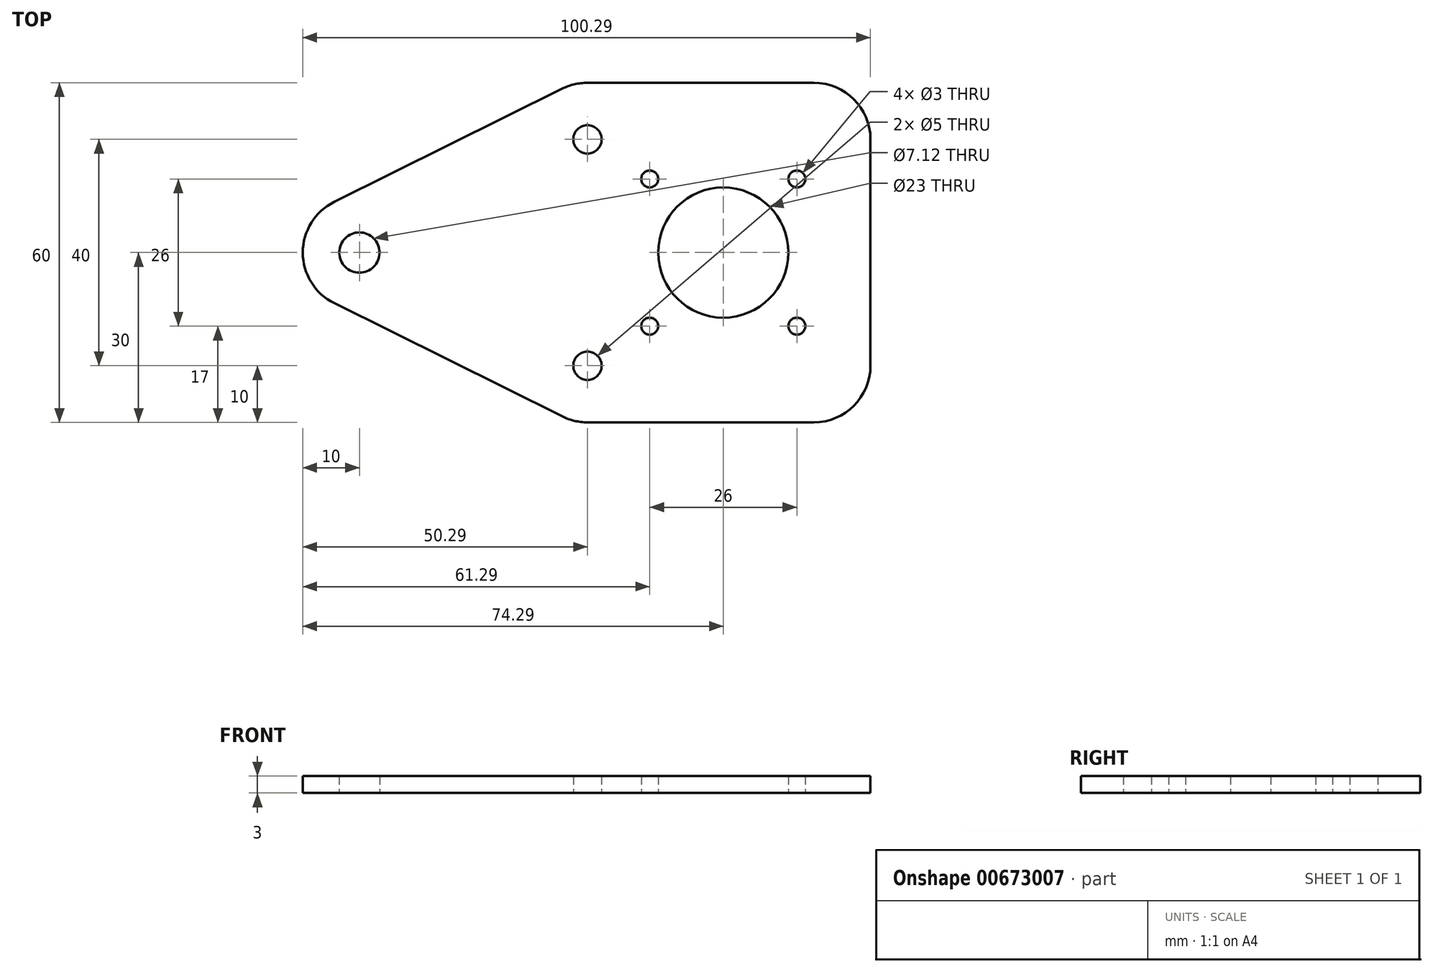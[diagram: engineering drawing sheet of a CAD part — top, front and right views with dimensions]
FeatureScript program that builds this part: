
annotation { "Feature Type Name" : "Feature", "Feature Type Description" : "" }
export const myFeature = defineFeature(function(context is Context, id is Id, definition is map)
    precondition{}
    {
        {
            var Q0;
            Q0=qCreatedBy(makeId("Top.planeOp"),FACE);
            var sketch = newSketch(context, id + "F0", { "sketchPlane" : qUnion([Q0])});
            skCircle(sketch, "E0", {"center": v(0, 0) * mm, "radius": 2.5 * mm});
            skCircle(sketch, "E1", {"center": v(0, 40) * mm, "radius": 2.5 * mm});
            skLineSegment(sketch, "E2", {"start": v(0, 40) * mm, "end": v(0, 0) * mm, "construction": true});
            skLineSegment(sketch, "E3", {"start": v(0, 20) * mm, "end": v(-40.3, 20) * mm, "construction": true});
            skCircle(sketch, "E4", {"center": v(-40.3, 20) * mm, "radius": 3.56 * mm});
            skArc(sketch, "E5", {"start": v(0, 50) * mm, "mid": v(-2.28, 49.74) * mm, "end": v(-4.45, 48.96) * mm});
            skArc(sketch, "E6", {"start": v(-4.45, -8.96) * mm, "mid": v(-2.28, -9.74) * mm, "end": v(0, -10) * mm});
            skArc(sketch, "E7", {"start": v(-44.74, 28.96) * mm, "mid": v(-50.3, 20) * mm, "end": v(-44.74, 11.04) * mm});
            skLineSegment(sketch, "E8", {"start": v(-44.74, 28.96) * mm, "end": v(-4.45, 48.96) * mm});
            skLineSegment(sketch, "E9", {"start": v(-44.74, 11.04) * mm, "end": v(-4.45, -8.96) * mm});
            skLineSegment(sketch, "E10", {"start": v(0, 40) * mm, "end": v(40, 40) * mm, "construction": true});
            skLineSegment(sketch, "E11", {"start": v(0, 0) * mm, "end": v(40, 0) * mm, "construction": true});
            skArc(sketch, "E12", {"start": v(50, 40) * mm, "mid": v(47.07, 47.07) * mm, "end": v(40, 50) * mm});
            skArc(sketch, "E13", {"start": v(40, -10) * mm, "mid": v(47.07, -7.07) * mm, "end": v(50, 0) * mm});
            skLineSegment(sketch, "E14", {"start": v(0, 50) * mm, "end": v(40, 50) * mm});
            skLineSegment(sketch, "E15", {"start": v(50, 40) * mm, "end": v(50, 0) * mm});
            skLineSegment(sketch, "E16", {"start": v(0, -10) * mm, "end": v(40, -10) * mm});
            skCircle(sketch, "E17", {"center": v(24, 20) * mm, "radius": 11.5 * mm});
            skCircle(sketch, "E18", {"center": v(37, 33) * mm, "radius": 1.5 * mm});
            skCircle(sketch, "E19.1.0", {"center": v(11, 33) * mm, "radius": 1.5 * mm});
            skCircle(sketch, "E19.2.0", {"center": v(11, 7) * mm, "radius": 1.5 * mm});
            skCircle(sketch, "E19.3.0", {"center": v(37, 7) * mm, "radius": 1.5 * mm});
            skSolve(sketch);
        }
        {
            var Q0;
            Q0=makeQuery(id+"F0.imprint","IMPRINT",FACE,{"disambiguationData":[TD([[makeQuery(id+"F0.imprint","IMPRINT",EDGE,{"derivedFrom":sQuery(id+"F0.wireOp",EDGE,"E0")}),-1.0]])]});
            extrude(context, id + "F1", {"entities" : qUnion([Q0]), "depth" : 3 * mm, "offsetDistance" : 25 * mm});
        }
    });
